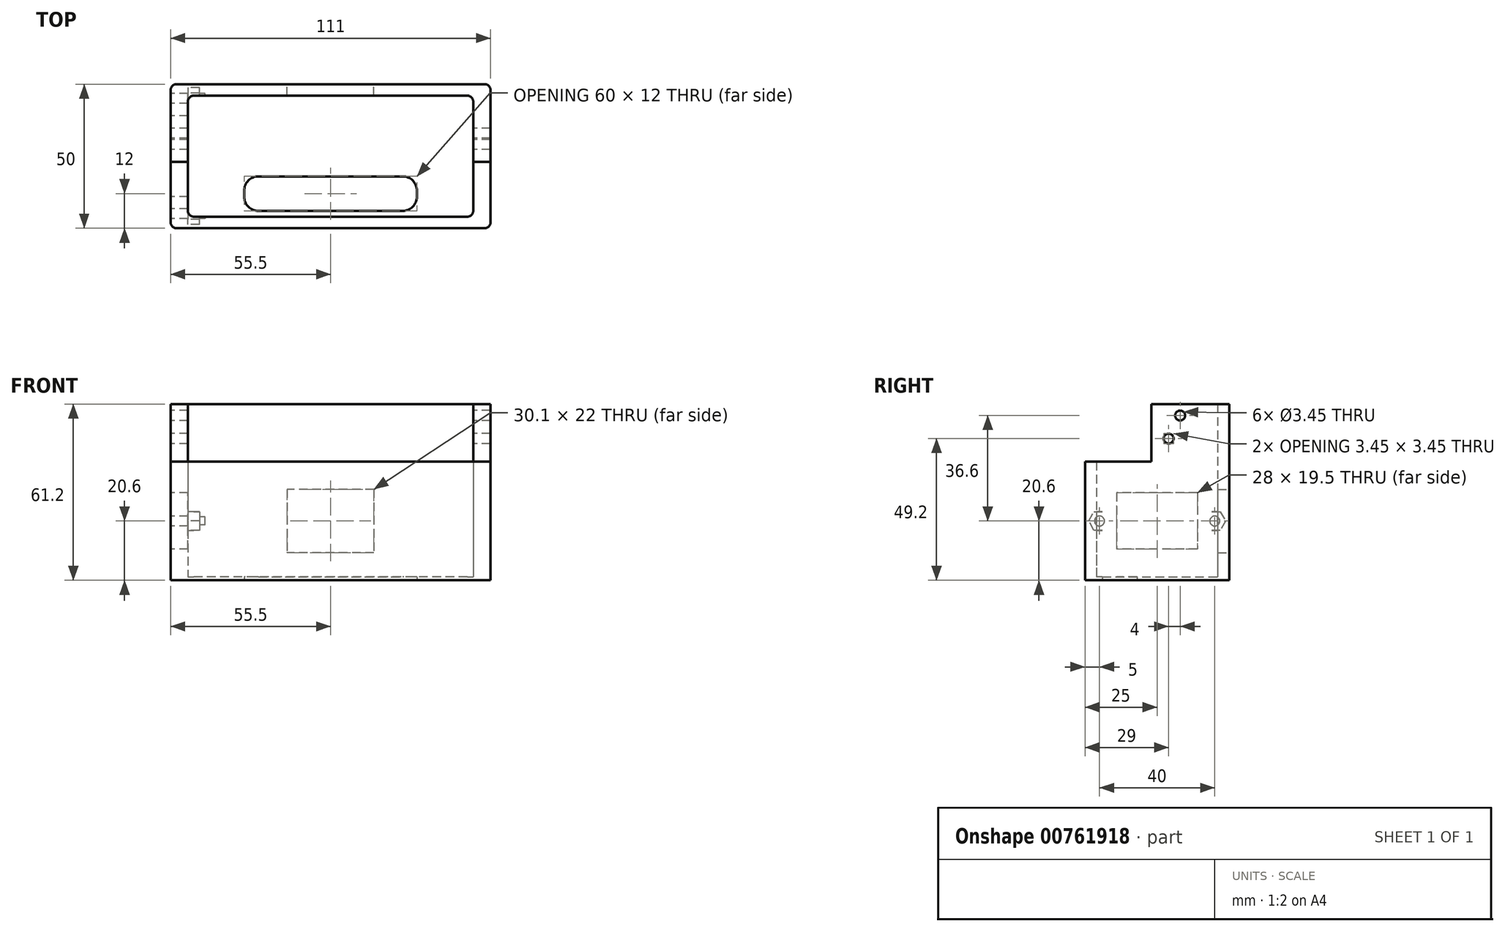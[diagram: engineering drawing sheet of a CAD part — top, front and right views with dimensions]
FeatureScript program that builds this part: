
annotation { "Feature Type Name" : "Feature", "Feature Type Description" : "" }
export const myFeature = defineFeature(function(context is Context, id is Id, definition is map)
    precondition{}
    {
        {
            var Q0;
            Q0=qCreatedBy(makeId("Top.planeOp"),FACE);
            var sketch = newSketch(context, id + "F0", { "sketchPlane" : qUnion([Q0])});
            skLineSegment(sketch, "E0.bottom", {"start": v(0, 0) * mm, "end": v(111, 0) * mm});
            skLineSegment(sketch, "E0.top", {"start": v(0, 50) * mm, "end": v(111, 50) * mm});
            skLineSegment(sketch, "E0.left", {"start": v(0, 0) * mm, "end": v(0, 50) * mm});
            skLineSegment(sketch, "E0.right", {"start": v(111, 0) * mm, "end": v(111, 50) * mm});
            skLineSegment(sketch, "E1.bottom", {"start": v(6, 46) * mm, "end": v(105, 46) * mm});
            skLineSegment(sketch, "E1.top", {"start": v(6, 4) * mm, "end": v(105, 4) * mm});
            skLineSegment(sketch, "E1.left", {"start": v(6, 46) * mm, "end": v(6, 4) * mm});
            skLineSegment(sketch, "E1.right", {"start": v(105, 46) * mm, "end": v(105, 4) * mm});
            skLineSegment(sketch, "E2.bottom", {"start": v(30.5, 18) * mm, "end": v(80.5, 18) * mm});
            skLineSegment(sketch, "E2.top", {"start": v(30.5, 6) * mm, "end": v(80.5, 6) * mm});
            skLineSegment(sketch, "E2.left", {"start": v(25.5, 13) * mm, "end": v(25.5, 11) * mm});
            skLineSegment(sketch, "E2.right", {"start": v(85.5, 13) * mm, "end": v(85.5, 11) * mm});
            skLineSegment(sketch, "E3", {"start": v(55.5, 4) * mm, "end": v(55.5, 6) * mm, "construction": true});
            skPoint(sketch, "E4.visualSharp", {"position": v(25.5, 18) * mm});
            skArc(sketch, "E4.filletArc", {"start": v(30.5, 18) * mm, "mid": v(26.96, 16.54) * mm, "end": v(25.5, 13) * mm});
            skPoint(sketch, "E5.visualSharp", {"position": v(25.5, 6) * mm});
            skArc(sketch, "E5.filletArc", {"start": v(25.5, 11) * mm, "mid": v(26.96, 7.46) * mm, "end": v(30.5, 6) * mm});
            skPoint(sketch, "E6.visualSharp", {"position": v(85.5, 18) * mm});
            skArc(sketch, "E6.filletArc", {"start": v(85.5, 13) * mm, "mid": v(84.04, 16.54) * mm, "end": v(80.5, 18) * mm});
            skPoint(sketch, "E7.visualSharp", {"position": v(85.5, 6) * mm});
            skArc(sketch, "E7.filletArc", {"start": v(80.5, 6) * mm, "mid": v(84.04, 7.46) * mm, "end": v(85.5, 11) * mm});
            skSolve(sketch);
        }
        {
            var Q0;
            Q0 = qSketchRegion(id + "F0", true);
            var Q1;
            Q1=makeQuery(id+"F0.imprint","IMPRINT",FACE,{"disambiguationData":[TD([[makeQuery(id+"F0.imprint","IMPRINT",EDGE,{"derivedFrom":sQuery(id+"F0.wireOp",EDGE,"E1.bottom")}),-1.0]])]});
            extrude(context, id + "F1", {"entities" : qUnion([Q0, Q1]), "depth" : 1.2 * mm, "offsetDistance" : 25 * mm});
        }
        {
            var Q0;
            Q0 = qSketchRegion(id + "F0", true);
            extrude(context, id + "F2", {"entities" : qUnion([Q0]), "operationType" : NewBodyOperationType.ADD, "depth" : (1.2 + 40) * mm, "offsetDistance" : 25 * mm});
        }
        {
            var Q0;
            {var subQ0=sQuery(id+"F0.wireOp",EDGE,"E0.top");Q0=makeQuery(id+"F2.boolean.opBoolean","MERGE",FACE,{"derivedFrom":[makeQuery(id+"F1.opExtrude","SWEPT_FACE",FACE,{"disambiguationData":[OSD([subQ0])]}),makeQuery(id+"F2.opExtrude","SWEPT_FACE",FACE,{"disambiguationData":[OSD([subQ0])]})]});}
            var sketch = newSketch(context, id + "F3", { "sketchPlane" : qUnion([Q0])});
            skLineSegment(sketch, "E8.bottom", {"start": v(-70.55, 31.6) * mm, "end": v(-40.45, 31.6) * mm});
            skLineSegment(sketch, "E8.top", {"start": v(-70.55, 9.6) * mm, "end": v(-40.45, 9.6) * mm});
            skLineSegment(sketch, "E8.left", {"start": v(-70.55, 31.6) * mm, "end": v(-70.55, 9.6) * mm});
            skLineSegment(sketch, "E8.right", {"start": v(-40.45, 31.6) * mm, "end": v(-40.45, 9.6) * mm});
            skLineSegment(sketch, "E9", {"start": v(-55.5, 0) * mm, "end": v(-55.5, 9.6) * mm, "construction": true});
            skLineSegment(sketch, "E10", {"start": v(-111, 20.6) * mm, "end": v(-70.55, 20.6) * mm, "construction": true});
            skSolve(sketch);
        }
        {
            var Q0;
            Q0 = qSketchRegion(id + "F3", true);
            extrude(context, id + "F4", {"entities" : qUnion([Q0]), "operationType" : NewBodyOperationType.REMOVE, "oppositeDirection" : true, "depth" : 4 * mm, "offsetDistance" : 25 * mm});
        }
        {
            var Q0;
            Q0=makeQuery(id+"F2.opExtrude","CAP_FACE",FACE,{"disambiguationData":[OSD([sQuery(id+"F0.wireOp",EDGE,"E0.bottom"),sQuery(id+"F0.wireOp",EDGE,"E0.top"),sQuery(id+"F0.wireOp",EDGE,"E0.left"),sQuery(id+"F0.wireOp",EDGE,"E0.right"),sQuery(id+"F0.wireOp",EDGE,"E1.bottom"),sQuery(id+"F0.wireOp",EDGE,"E1.top"),sQuery(id+"F0.wireOp",EDGE,"E1.left"),sQuery(id+"F0.wireOp",EDGE,"E1.right")])],"isStart":false});
            var sketch = newSketch(context, id + "F5", { "sketchPlane" : qUnion([Q0])});
            skLineSegment(sketch, "E11", {"start": v(0, 23) * mm, "end": v(6, 23) * mm});
            skLineSegment(sketch, "E12", {"start": v(6, 23) * mm, "end": v(6, 46) * mm});
            skLineSegment(sketch, "E13", {"start": v(6, 46) * mm, "end": v(105, 46) * mm});
            skLineSegment(sketch, "E14", {"start": v(105, 46) * mm, "end": v(105, 23) * mm});
            skLineSegment(sketch, "E15", {"start": v(105, 23) * mm, "end": v(111, 23) * mm});
            skLineSegment(sketch, "E16", {"start": v(111, 23) * mm, "end": v(111, 50) * mm});
            skLineSegment(sketch, "E17", {"start": v(111, 50) * mm, "end": v(0, 50) * mm});
            skLineSegment(sketch, "E18", {"start": v(0, 50) * mm, "end": v(0, 23) * mm});
            skSolve(sketch);
        }
        {
            var Q0;
            Q0 = qSketchRegion(id + "F5", true);
            extrude(context, id + "F6", {"entities" : qUnion([Q0]), "operationType" : NewBodyOperationType.ADD, "depth" : 20 * mm, "offsetDistance" : 25 * mm});
        }
        {
            var Q0;
            {var subQ0=sQuery(id+"F0.wireOp",EDGE,"E0.left");Q0=makeQuery(id+"F2.boolean.opBoolean","MERGE",FACE,{"derivedFrom":[makeQuery(id+"F1.opExtrude","SWEPT_FACE",FACE,{"disambiguationData":[OSD([subQ0])]}),makeQuery(id+"F2.opExtrude","SWEPT_FACE",FACE,{"disambiguationData":[OSD([subQ0])]})]});}
            var sketch = newSketch(context, id + "F7", { "sketchPlane" : qUnion([Q0])});
            skLineSegment(sketch, "E19.bottom", {"start": v(-39, 30.35) * mm, "end": v(-11, 30.35) * mm});
            skLineSegment(sketch, "E19.top", {"start": v(-39, 10.85) * mm, "end": v(-11, 10.85) * mm});
            skLineSegment(sketch, "E19.left", {"start": v(-39, 30.35) * mm, "end": v(-39, 10.85) * mm});
            skLineSegment(sketch, "E19.right", {"start": v(-11, 30.35) * mm, "end": v(-11, 10.85) * mm});
            skLineSegment(sketch, "E20", {"start": v(-25, 0) * mm, "end": v(-25, 10.85) * mm, "construction": true});
            skLineSegment(sketch, "E21", {"start": v(-11, 20.6) * mm, "end": v(0, 20.6) * mm, "construction": true});
            skCircle(sketch, "E22", {"center": v(-45, 20.6) * mm, "radius": 1.73 * mm});
            skCircle(sketch, "E23", {"center": v(-5, 20.6) * mm, "radius": 1.73 * mm});
            skLineSegment(sketch, "E24", {"start": v(-45, 20.6) * mm, "end": v(-5, 20.6) * mm, "construction": true});
            skLineSegment(sketch, "E25", {"start": v(-25, 10.85) * mm, "end": v(-25, 20.6) * mm, "construction": true});
            skCircle(sketch, "E26", {"center": v(-29, 49.2) * mm, "radius": 1.73 * mm});
            skCircle(sketch, "E27", {"center": v(-33, 57.2) * mm, "radius": 1.73 * mm});
            skSolve(sketch);
        }
        {
            var Q0;
            Q0=makeQuery(id+"F7.imprint","IMPRINT",FACE,{"disambiguationData":[TD([[makeQuery(id+"F7.imprint","IMPRINT",EDGE,{"derivedFrom":sQuery(id+"F7.wireOp",EDGE,"gh1StohQ-Vrfs-J08P-nW3H-ZPxFOxHRp2NL")}),1.0]])]});
            var Q1;
            Q1=makeQuery(id+"F7.imprint","IMPRINT",FACE,{"disambiguationData":[TD([[makeQuery(id+"F7.imprint","IMPRINT",EDGE,{"derivedFrom":sQuery(id+"F7.wireOp",EDGE,"E26")}),1.0]])]});
            var Q2;
            Q2=makeQuery(id+"F7.imprint","IMPRINT",FACE,{"disambiguationData":[TD([[makeQuery(id+"F7.imprint","IMPRINT",EDGE,{"derivedFrom":sQuery(id+"F7.wireOp",EDGE,"E27")}),1.0]])]});
            extrude(context, id + "F8", {"entities" : qUnion([Q0, Q1, Q2]), "operationType" : NewBodyOperationType.REMOVE, "oppositeDirection" : true, "depth" : 114.6 * mm, "offsetDistance" : 25 * mm});
        }
        {
            var Q0;
            Q0=makeQuery(id+"F7.imprint","IMPRINT",FACE,{"disambiguationData":[TD([[makeQuery(id+"F7.imprint","IMPRINT",EDGE,{"derivedFrom":sQuery(id+"F7.wireOp",EDGE,"E19.bottom")}),-1.0]])]});
            var Q1;
            Q1=makeQuery(id+"F7.imprint","IMPRINT",FACE,{"disambiguationData":[TD([[makeQuery(id+"F7.imprint","IMPRINT",EDGE,{"derivedFrom":sQuery(id+"F7.wireOp",EDGE,"E22")}),1.0]])]});
            var Q2;
            Q2=makeQuery(id+"F7.imprint","IMPRINT",FACE,{"disambiguationData":[TD([[makeQuery(id+"F7.imprint","IMPRINT",EDGE,{"derivedFrom":sQuery(id+"F7.wireOp",EDGE,"E23")}),1.0]])]});
            extrude(context, id + "F9", {"entities" : qUnion([Q0, Q1, Q2]), "operationType" : NewBodyOperationType.REMOVE, "oppositeDirection" : true, "depth" : 12 * mm, "offsetDistance" : 25 * mm});
        }
        {
            var Q0;
            Q0=makeQuery(id+"F2.opExtrude","SWEPT_FACE",FACE,{"disambiguationData":[OSD([sQuery(id+"F0.wireOp",EDGE,"E1.left")])]});
            var sketch = newSketch(context, id + "F10", { "sketchPlane" : qUnion([Q0])});
            skCircle(sketch, "E28.cCircle", {"center": v(5, 20.6) * mm, "radius": 3.25 * mm, "construction": true});
            skLineSegment(sketch, "E28.0", {"start": v(6.88, 23.85) * mm, "end": v(8.75, 20.6) * mm});
            skLineSegment(sketch, "E28.1", {"start": v(8.75, 20.6) * mm, "end": v(6.88, 17.35) * mm});
            skLineSegment(sketch, "E28.2", {"start": v(6.88, 17.35) * mm, "end": v(3.12, 17.35) * mm});
            skLineSegment(sketch, "E28.3", {"start": v(3.12, 17.35) * mm, "end": v(1.25, 20.6) * mm});
            skLineSegment(sketch, "E28.4", {"start": v(1.25, 20.6) * mm, "end": v(3.12, 23.85) * mm});
            skLineSegment(sketch, "E28.5", {"start": v(3.12, 23.85) * mm, "end": v(6.88, 23.85) * mm});
            skPoint(sketch, "E28.0.midPoint", {"position": v(7.81, 22.23) * mm});
            skCircle(sketch, "E29.cCircle", {"center": v(45, 20.6) * mm, "radius": 3.25 * mm, "construction": true});
            skLineSegment(sketch, "E29.0", {"start": v(41.25, 20.6) * mm, "end": v(43.12, 23.85) * mm});
            skLineSegment(sketch, "E29.1", {"start": v(43.12, 23.85) * mm, "end": v(46.88, 23.85) * mm});
            skLineSegment(sketch, "E29.2", {"start": v(46.88, 23.85) * mm, "end": v(48.75, 20.6) * mm});
            skLineSegment(sketch, "E29.3", {"start": v(48.75, 20.6) * mm, "end": v(46.88, 17.35) * mm});
            skLineSegment(sketch, "E29.4", {"start": v(46.88, 17.35) * mm, "end": v(43.12, 17.35) * mm});
            skLineSegment(sketch, "E29.5", {"start": v(43.12, 17.35) * mm, "end": v(41.25, 20.6) * mm});
            skPoint(sketch, "E29.0.midPoint", {"position": v(42.19, 22.22) * mm});
            skSolve(sketch);
        }
        {
            var Q0;
            Q0 = qSketchRegion(id + "F10", true);
            extrude(context, id + "F11", {"entities" : qUnion([Q0]), "operationType" : NewBodyOperationType.REMOVE, "depth" : 4 * mm, "offsetDistance" : 25 * mm});
        }
        {
            var Q0;
            {var subQ0=sQuery(id+"F5.wireOp",EDGE,"E13");var subQ1=sQuery(id+"F5.wireOp",EDGE,"E12");var subQ2=sQuery(id+"F0.wireOp",EDGE,"E1.left");var subQ3=sQuery(id+"F0.wireOp",EDGE,"E1.bottom");Q0=makeQuery(id+"F9.boolean.opBoolean","SPLIT",EDGE,{"disambiguationData":[TD([makeQuery(id+"F6.opExtrude","CAP_FACE",FACE,{"disambiguationData":[OSD([sQuery(id+"F5.wireOp",EDGE,"E11"),subQ1,subQ0,sQuery(id+"F5.wireOp",EDGE,"E14"),sQuery(id+"F5.wireOp",EDGE,"E15"),sQuery(id+"F5.wireOp",EDGE,"E16"),sQuery(id+"F5.wireOp",EDGE,"E17"),sQuery(id+"F5.wireOp",EDGE,"E18")])],"isStart":false})])],"derivedFrom":makeQuery(id+"F6.boolean.opBoolean","MERGE",EDGE,{"derivedFrom":[makeQuery(id+"F2.opExtrude","SWEPT_EDGE",EDGE,{"disambiguationData":[OSD([subQ3,subQ2])]}),makeQuery(id+"F6.opExtrude","SWEPT_EDGE",EDGE,{"disambiguationData":[OSD([subQ1,subQ0])]})]})});}
            var Q1;
            {var subQ0=sQuery(id+"F0.wireOp",EDGE,"E1.left");var subQ1=sQuery(id+"F5.wireOp",EDGE,"E12");var subQ2=sQuery(id+"F0.wireOp",EDGE,"E1.bottom");var subQ3=sQuery(id+"F5.wireOp",EDGE,"E13");Q1=makeQuery(id+"F9.boolean.opBoolean","SPLIT",EDGE,{"disambiguationData":[TD([makeQuery(id+"F1.opExtrude","CAP_FACE",FACE,{"disambiguationData":[OSD([sQuery(id+"F0.wireOp",EDGE,"E0.bottom"),sQuery(id+"F0.wireOp",EDGE,"E0.top"),sQuery(id+"F0.wireOp",EDGE,"E0.left"),sQuery(id+"F0.wireOp",EDGE,"E0.right"),sQuery(id+"F0.wireOp",EDGE,"E2.bottom"),sQuery(id+"F0.wireOp",EDGE,"E2.top"),sQuery(id+"F0.wireOp",EDGE,"E2.left"),sQuery(id+"F0.wireOp",EDGE,"E2.right"),sQuery(id+"F0.wireOp",EDGE,"E4.filletArc"),sQuery(id+"F0.wireOp",EDGE,"E5.filletArc"),sQuery(id+"F0.wireOp",EDGE,"E6.filletArc"),sQuery(id+"F0.wireOp",EDGE,"E7.filletArc")])],"isStart":false})])],"derivedFrom":makeQuery(id+"F6.boolean.opBoolean","MERGE",EDGE,{"derivedFrom":[makeQuery(id+"F2.opExtrude","SWEPT_EDGE",EDGE,{"disambiguationData":[OSD([subQ2,subQ0])]}),makeQuery(id+"F6.opExtrude","SWEPT_EDGE",EDGE,{"disambiguationData":[OSD([subQ1,subQ3])]})]})});}
            var Q2;
            Q2=makeQuery(id+"F6.boolean.opBoolean","MERGE",EDGE,{"derivedFrom":[makeQuery(id+"F2.opExtrude","SWEPT_EDGE",EDGE,{"disambiguationData":[OSD([sQuery(id+"F0.wireOp",EDGE,"E1.bottom"),sQuery(id+"F0.wireOp",EDGE,"E1.right")])]}),makeQuery(id+"F6.opExtrude","SWEPT_EDGE",EDGE,{"disambiguationData":[OSD([sQuery(id+"F5.wireOp",EDGE,"E13"),sQuery(id+"F5.wireOp",EDGE,"E14")])]})]});
            var Q3;
            Q3=makeQuery(id+"F2.opExtrude","SWEPT_EDGE",EDGE,{"disambiguationData":[OSD([sQuery(id+"F0.wireOp",EDGE,"E1.top"),sQuery(id+"F0.wireOp",EDGE,"E1.right")])]});
            var Q4;
            {var subQ0=sQuery(id+"F0.wireOp",EDGE,"E1.left");var subQ1=sQuery(id+"F0.wireOp",EDGE,"E1.top");Q4=makeQuery(id+"F9.boolean.opBoolean","SPLIT",EDGE,{"disambiguationData":[TD([makeQuery(id+"F2.opExtrude","CAP_FACE",FACE,{"disambiguationData":[OSD([sQuery(id+"F0.wireOp",EDGE,"E0.bottom"),sQuery(id+"F0.wireOp",EDGE,"E0.top"),sQuery(id+"F0.wireOp",EDGE,"E0.left"),sQuery(id+"F0.wireOp",EDGE,"E0.right"),sQuery(id+"F0.wireOp",EDGE,"E1.bottom"),subQ1,subQ0,sQuery(id+"F0.wireOp",EDGE,"E1.right")])],"isStart":false})])],"derivedFrom":makeQuery(id+"F2.opExtrude","SWEPT_EDGE",EDGE,{"disambiguationData":[OSD([subQ1,subQ0])]})});}
            var Q5;
            {var subQ0=sQuery(id+"F0.wireOp",EDGE,"E1.left");var subQ1=sQuery(id+"F0.wireOp",EDGE,"E1.top");Q5=makeQuery(id+"F9.boolean.opBoolean","SPLIT",EDGE,{"disambiguationData":[TD([makeQuery(id+"F1.opExtrude","CAP_FACE",FACE,{"disambiguationData":[OSD([sQuery(id+"F0.wireOp",EDGE,"E0.bottom"),sQuery(id+"F0.wireOp",EDGE,"E0.top"),sQuery(id+"F0.wireOp",EDGE,"E0.left"),sQuery(id+"F0.wireOp",EDGE,"E0.right"),sQuery(id+"F0.wireOp",EDGE,"E2.bottom"),sQuery(id+"F0.wireOp",EDGE,"E2.top"),sQuery(id+"F0.wireOp",EDGE,"E2.left"),sQuery(id+"F0.wireOp",EDGE,"E2.right"),sQuery(id+"F0.wireOp",EDGE,"E4.filletArc"),sQuery(id+"F0.wireOp",EDGE,"E5.filletArc"),sQuery(id+"F0.wireOp",EDGE,"E6.filletArc"),sQuery(id+"F0.wireOp",EDGE,"E7.filletArc")])],"isStart":false})])],"derivedFrom":makeQuery(id+"F2.opExtrude","SWEPT_EDGE",EDGE,{"disambiguationData":[OSD([subQ1,subQ0])]})});}
            var Q6;
            {var subQ0=sQuery(id+"F0.wireOp",EDGE,"E0.right");var subQ1=sQuery(id+"F0.wireOp",EDGE,"E0.bottom");Q6=makeQuery(id+"F2.boolean.opBoolean","MERGE",EDGE,{"derivedFrom":[makeQuery(id+"F1.opExtrude","SWEPT_EDGE",EDGE,{"disambiguationData":[OSD([subQ1,subQ0])]}),makeQuery(id+"F2.opExtrude","SWEPT_EDGE",EDGE,{"disambiguationData":[OSD([subQ1,subQ0])]})]});}
            var Q7;
            {var subQ0=sQuery(id+"F0.wireOp",EDGE,"E0.right");var subQ1=sQuery(id+"F0.wireOp",EDGE,"E0.top");Q7=makeQuery(id+"F6.boolean.opBoolean","MERGE",EDGE,{"derivedFrom":[makeQuery(id+"F2.boolean.opBoolean","MERGE",EDGE,{"derivedFrom":[makeQuery(id+"F1.opExtrude","SWEPT_EDGE",EDGE,{"disambiguationData":[OSD([subQ1,subQ0])]}),makeQuery(id+"F2.opExtrude","SWEPT_EDGE",EDGE,{"disambiguationData":[OSD([subQ1,subQ0])]})]}),makeQuery(id+"F6.opExtrude","SWEPT_EDGE",EDGE,{"disambiguationData":[OSD([sQuery(id+"F5.wireOp",EDGE,"E16"),sQuery(id+"F5.wireOp",EDGE,"E17")])]})]});}
            var Q8;
            {var subQ0=sQuery(id+"F0.wireOp",EDGE,"E0.left");var subQ1=sQuery(id+"F0.wireOp",EDGE,"E0.top");Q8=makeQuery(id+"F6.boolean.opBoolean","MERGE",EDGE,{"derivedFrom":[makeQuery(id+"F2.boolean.opBoolean","MERGE",EDGE,{"derivedFrom":[makeQuery(id+"F1.opExtrude","SWEPT_EDGE",EDGE,{"disambiguationData":[OSD([subQ1,subQ0])]}),makeQuery(id+"F2.opExtrude","SWEPT_EDGE",EDGE,{"disambiguationData":[OSD([subQ1,subQ0])]})]}),makeQuery(id+"F6.opExtrude","SWEPT_EDGE",EDGE,{"disambiguationData":[OSD([sQuery(id+"F5.wireOp",EDGE,"E17"),sQuery(id+"F5.wireOp",EDGE,"E18")])]})]});}
            var Q9;
            {var subQ0=sQuery(id+"F0.wireOp",EDGE,"E0.left");var subQ1=sQuery(id+"F0.wireOp",EDGE,"E0.bottom");Q9=makeQuery(id+"F2.boolean.opBoolean","MERGE",EDGE,{"derivedFrom":[makeQuery(id+"F1.opExtrude","SWEPT_EDGE",EDGE,{"disambiguationData":[OSD([subQ1,subQ0])]}),makeQuery(id+"F2.opExtrude","SWEPT_EDGE",EDGE,{"disambiguationData":[OSD([subQ1,subQ0])]})]});}
            fillet(context, id + "F12", {"entities" : qUnion([Q0, Q1, Q2, Q3, Q4, Q5, Q6, Q7, Q8, Q9]), "radius" : 2 * mm, "tangentPropagation" : true, "allowEdgeOverflow" : false});
        }
    });
